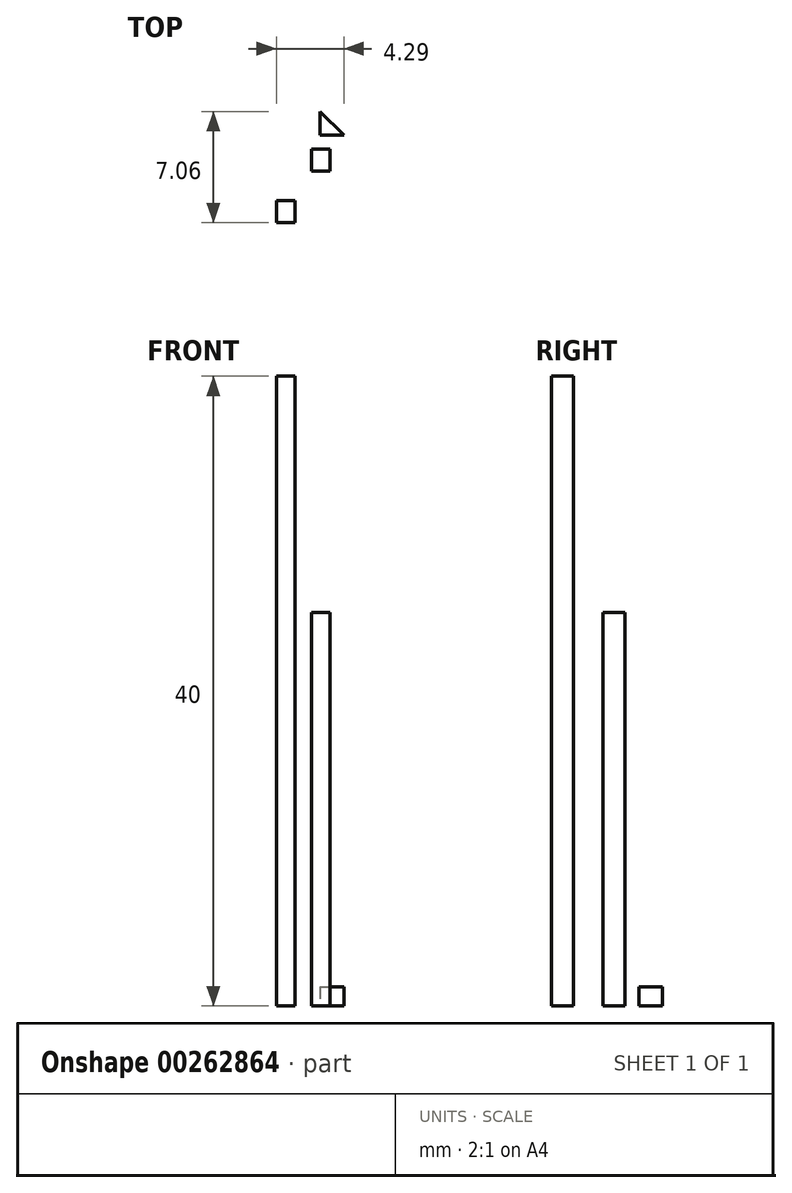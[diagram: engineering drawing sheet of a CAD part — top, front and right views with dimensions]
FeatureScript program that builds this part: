
annotation { "Feature Type Name" : "Feature", "Feature Type Description" : "" }
export const myFeature = defineFeature(function(context is Context, id is Id, definition is map)
    precondition{}
    {
        {
            var Q0;
            Q0=qCreatedBy(makeId("Top.planeOp"),FACE);
            var sketch = newSketch(context, id + "F0", { "sketchPlane" : qUnion([Q0])});
            skLineSegment(sketch, "E0.bottom", {"start": v(0.6, -0.7) * mm, "end": v(-0.6, -0.7) * mm});
            skLineSegment(sketch, "E0.top", {"start": v(0.6, 0.7) * mm, "end": v(-0.6, 0.7) * mm});
            skLineSegment(sketch, "E0.left", {"start": v(0.6, -0.7) * mm, "end": v(0.6, 0.7) * mm});
            skLineSegment(sketch, "E0.right", {"start": v(-0.6, -0.7) * mm, "end": v(-0.6, 0.7) * mm});
            skPoint(sketch, "E0.middle", {"position": v(0, 0) * mm});
            skSolve(sketch);
        }
        {
            var Q0;
            Q0=makeQuery(id+"F0.imprint","IMPRINT",FACE,{"disambiguationData":[TD([[makeQuery(id+"F0.imprint","IMPRINT",EDGE,{"derivedFrom":sQuery(id+"F0.wireOp",EDGE,"E0.bottom")}),-1.0]])]});
            var sketch = newSketch(context, id + "F1", { "sketchPlane" : qUnion([Q0])});
            skSolve(sketch);
        }
        {
            var Q0;
            Q0 = qSketchRegion(id + "F1", true);
            var Q1;
            Q1=makeQuery(id+"F0.imprint","IMPRINT",FACE,{"disambiguationData":[TD([[makeQuery(id+"F0.imprint","IMPRINT",EDGE,{"derivedFrom":sQuery(id+"F0.wireOp",EDGE,"E0.bottom")}),-1.0]])]});
            extrude(context, id + "F2", {"entities" : qUnion([Q0, Q1]), "depth" : 40 * mm});
        }
        {
            var Q0;
            Q0=qCreatedBy(makeId("Top.planeOp"),FACE);
            var sketch = newSketch(context, id + "F3", { "sketchPlane" : qUnion([Q0])});
            skLineSegment(sketch, "E1.bottom", {"start": v(1.62, 3.98) * mm, "end": v(2.82, 3.98) * mm});
            skLineSegment(sketch, "E1.top", {"start": v(1.62, 2.58) * mm, "end": v(2.82, 2.58) * mm});
            skLineSegment(sketch, "E1.left", {"start": v(1.62, 3.98) * mm, "end": v(1.62, 2.58) * mm});
            skLineSegment(sketch, "E1.right", {"start": v(2.82, 3.98) * mm, "end": v(2.82, 2.58) * mm});
            skLineSegment(sketch, "E2.bottom", {"start": v(2.04, -1.05) * mm, "end": v(3.24, -1.05) * mm});
            skLineSegment(sketch, "E2.top", {"start": v(2.04, -2.45) * mm, "end": v(3.24, -2.45) * mm});
            skLineSegment(sketch, "E2.left", {"start": v(2.04, -1.05) * mm, "end": v(2.04, -2.45) * mm});
            skLineSegment(sketch, "E2.right", {"start": v(3.24, -1.05) * mm, "end": v(3.24, -2.45) * mm});
            skLineSegment(sketch, "E3.bottom", {"start": v(4.25, 3.78) * mm, "end": v(5.45, 3.78) * mm});
            skLineSegment(sketch, "E3.top", {"start": v(4.25, 2.38) * mm, "end": v(5.45, 2.38) * mm});
            skLineSegment(sketch, "E3.left", {"start": v(4.25, 3.78) * mm, "end": v(4.25, 2.38) * mm});
            skLineSegment(sketch, "E3.right", {"start": v(5.45, 3.78) * mm, "end": v(5.45, 2.38) * mm});
            skLineSegment(sketch, "E4.bottom", {"start": v(4.74, -1.01) * mm, "end": v(5.94, -1.01) * mm});
            skLineSegment(sketch, "E4.top", {"start": v(4.74, -2.41) * mm, "end": v(5.94, -2.41) * mm});
            skLineSegment(sketch, "E4.left", {"start": v(4.74, -1.01) * mm, "end": v(4.74, -2.41) * mm});
            skLineSegment(sketch, "E4.right", {"start": v(5.94, -1.01) * mm, "end": v(5.94, -2.41) * mm});
            skSolve(sketch);
        }
        {
            var Q0;
            Q0=makeQuery(id+"F3.imprint","IMPRINT",FACE,{"disambiguationData":[TD([[makeQuery(id+"F3.imprint","IMPRINT",EDGE,{"derivedFrom":sQuery(id+"F3.wireOp",EDGE,"E1.bottom")}),-1.0]])]});
            extrude(context, id + "F4", {"entities" : qUnion([Q0]), "depth" : 25 * mm});
        }
        {
            var Q0;
            Q0=qCreatedBy(makeId("Top.planeOp"),FACE);
            var sketch = newSketch(context, id + "F5", { "sketchPlane" : qUnion([Q0])});
            skLineSegment(sketch, "E5", {"start": v(2.19, 6.36) * mm, "end": v(2.19, 4.86) * mm});
            skLineSegment(sketch, "E6", {"start": v(2.19, 4.86) * mm, "end": v(3.69, 4.86) * mm});
            skLineSegment(sketch, "E7", {"start": v(2.19, 6.36) * mm, "end": v(3.69, 4.86) * mm});
            skSolve(sketch);
        }
        {
            var Q0;
            Q0=makeQuery(id+"F5.imprint","IMPRINT",FACE,{"disambiguationData":[TD([[makeQuery(id+"F5.imprint","IMPRINT",EDGE,{"derivedFrom":sQuery(id+"F5.wireOp",EDGE,"E5")}),1.0]])]});
            extrude(context, id + "F6", {"entities" : qUnion([Q0]), "depth" : 1.2 * mm});
        }
    });
